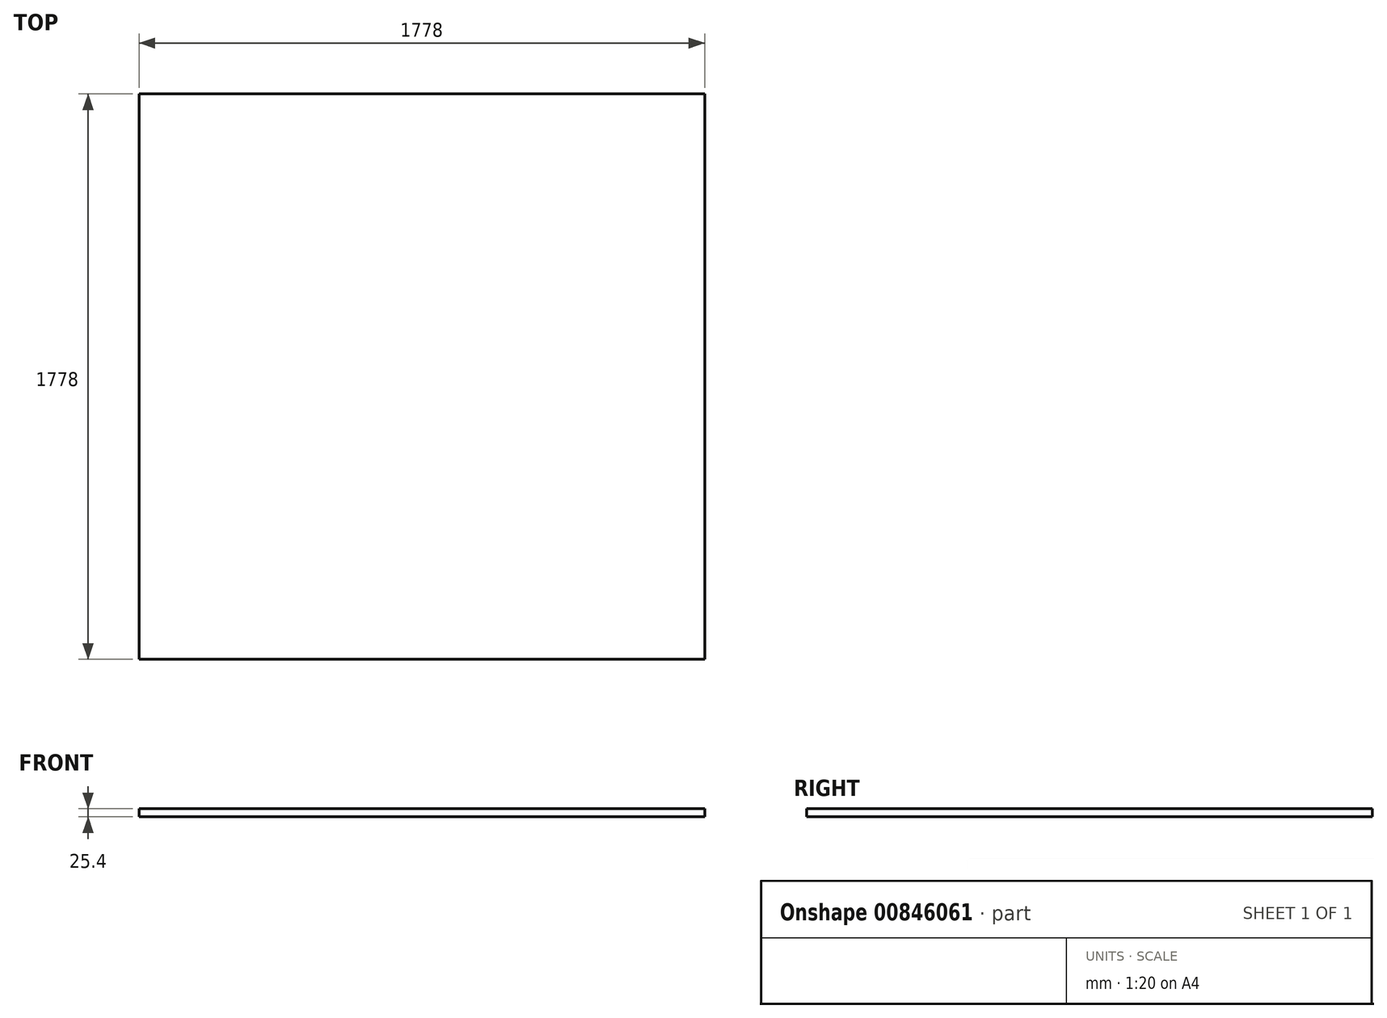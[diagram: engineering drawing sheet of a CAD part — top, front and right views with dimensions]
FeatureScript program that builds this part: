
annotation { "Feature Type Name" : "Feature", "Feature Type Description" : "" }
export const myFeature = defineFeature(function(context is Context, id is Id, definition is map)
    precondition{}
    {
        {
            var Q0;
            Q0=qCreatedBy(makeId("Top.planeOp"),FACE);
            var sketch = newSketch(context, id + "F0", { "sketchPlane" : qUnion([Q0])});
            skLineSegment(sketch, "E0.bottom", {"start": v(889, -889) * mm, "end": v(-889, -889) * mm});
            skLineSegment(sketch, "E0.top", {"start": v(889, 889) * mm, "end": v(-889, 889) * mm});
            skLineSegment(sketch, "E0.left", {"start": v(889, -889) * mm, "end": v(889, 889) * mm});
            skLineSegment(sketch, "E0.right", {"start": v(-889, -889) * mm, "end": v(-889, 889) * mm});
            skPoint(sketch, "E0.middle", {"position": v(0, 0) * mm});
            skSolve(sketch);
        }
        {
            var Q0;
            Q0 = qSketchRegion(id + "F0", true);
            extrude(context, id + "F1", {"entities" : qUnion([Q0]), "depth" : 25.4 * mm, "offsetDistance" : 25.4 * mm});
        }
    });
